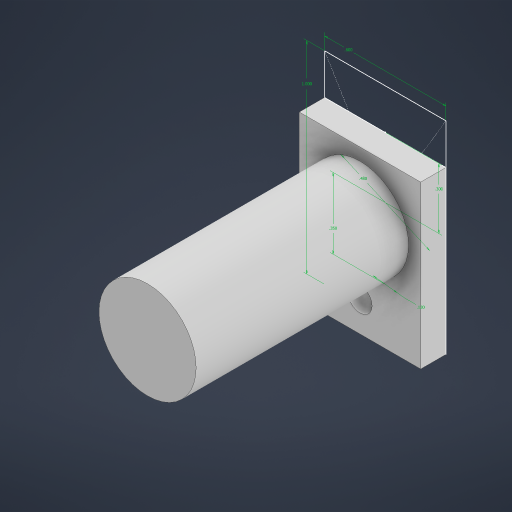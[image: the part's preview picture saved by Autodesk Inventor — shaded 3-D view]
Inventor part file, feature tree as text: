
AUTODESK INVENTOR PART (.ipt)
format: ipt  version: 2024.1 (Build 281209000, 209)  size: 194,048 bytes
history: native  units: in
note: dims shown in document units (in); Inventor stores cm internally (conversion verified against a paired STEP export)
features: extrude x2, sketch x1
ambient origin geometry x8: Origin, YZ Plane, XZ Plane, XY Plane, X Axis, Y Axis, Z Axis, Center Point
bodies: Solid1 (feature_tree)
feature tree (3):
  sketch  "Sketch1"  dims[d0=0.48in d1=0.6in d2=1.0in d3=0.125in d4=0.0in d5=1.05in d6=0.0in d7=0.12in d8=0.35in d10=0.3in]
  extrude  "Extrusion1"  Depth=0.6in
  extrude  "Extrusion2"  Depth=0.35in
